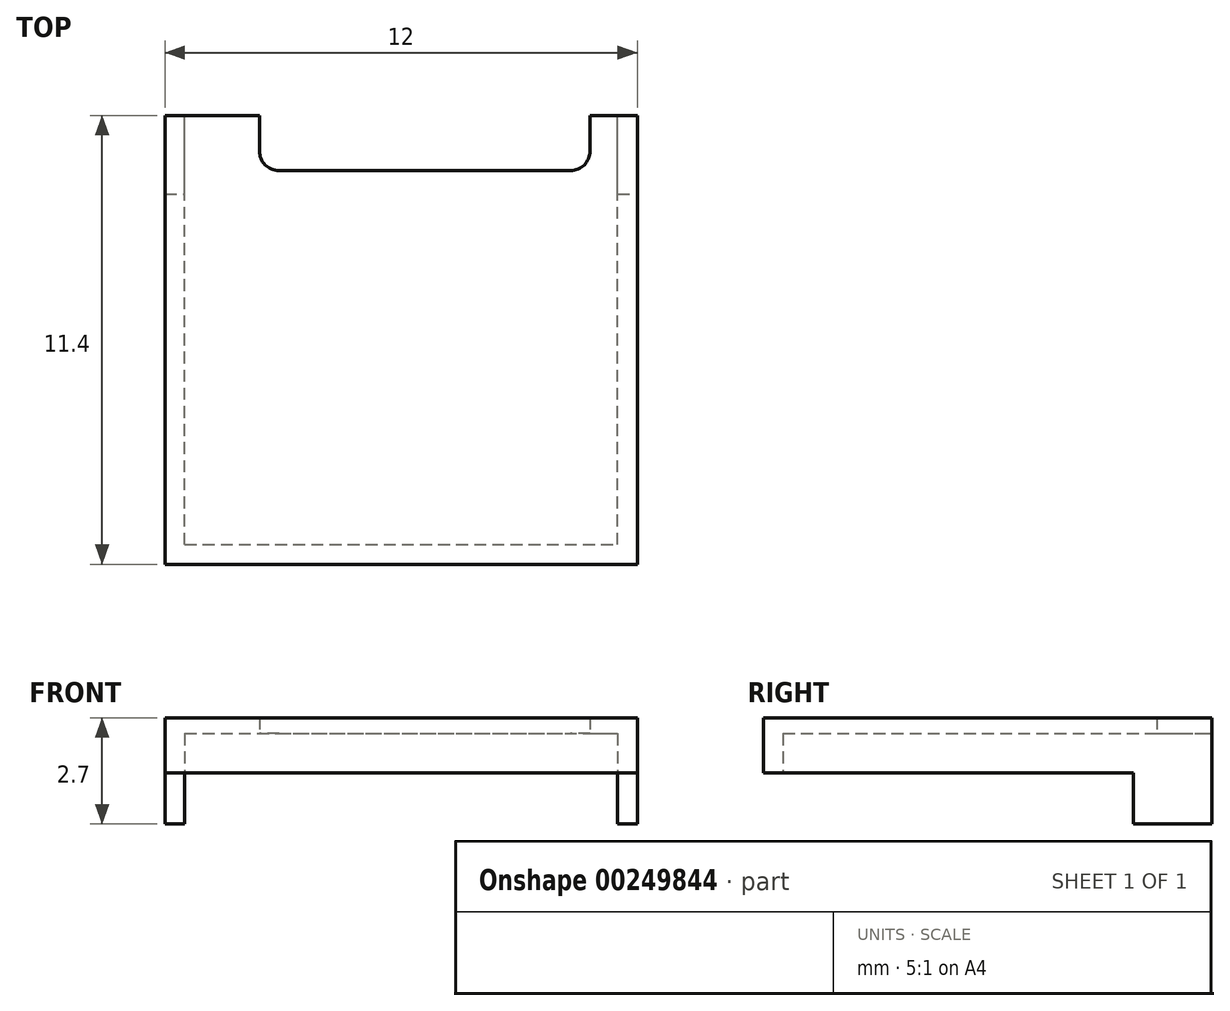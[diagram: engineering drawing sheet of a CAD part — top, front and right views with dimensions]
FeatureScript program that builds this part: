
annotation { "Feature Type Name" : "Feature", "Feature Type Description" : "" }
export const myFeature = defineFeature(function(context is Context, id is Id, definition is map)
    precondition{}
    {
        {
            var Q0;
            Q0=qCreatedBy(makeId("Top.planeOp"),FACE);
            var sketch = newSketch(context, id + "F0", { "sketchPlane" : qUnion([Q0])});
            skLineSegment(sketch, "E0.bottom", {"start": v(0, 0) * mm, "end": v(12, 0) * mm});
            skLineSegment(sketch, "E0.top", {"start": v(0, 11.4) * mm, "end": v(2.4, 11.4) * mm});
            skLineSegment(sketch, "E0.left", {"start": v(0, 0) * mm, "end": v(0, 11.4) * mm});
            skLineSegment(sketch, "E0.right", {"start": v(12, 0) * mm, "end": v(12, 11.4) * mm});
            skLineSegment(sketch, "E1", {"start": v(2.4, 11.4) * mm, "end": v(2.4, 10) * mm});
            skLineSegment(sketch, "E2", {"start": v(2.4, 10) * mm, "end": v(10.8, 10) * mm});
            skLineSegment(sketch, "E3", {"start": v(10.8, 10) * mm, "end": v(10.8, 11.4) * mm});
            skLineSegment(sketch, "E4.trimOffspring", {"start": v(10.8, 11.4) * mm, "end": v(12, 11.4) * mm});
            skSolve(sketch);
        }
        {
            var Q0;
            Q0 = qSketchRegion(id + "F0", true);
            extrude(context, id + "F1", {"entities" : qUnion([Q0]), "depth" : 1.4 * mm});
        }
        {
            var Q0;
            Q0=makeQuery(id+"F1.opExtrude","CAP_FACE",FACE,{"disambiguationData":[OSD([sQuery(id+"F0.wireOp",EDGE,"E0.bottom"),sQuery(id+"F0.wireOp",EDGE,"E0.top"),sQuery(id+"F0.wireOp",EDGE,"E0.left"),sQuery(id+"F0.wireOp",EDGE,"E0.right"),sQuery(id+"F0.wireOp",EDGE,"E1"),sQuery(id+"F0.wireOp",EDGE,"E2"),sQuery(id+"F0.wireOp",EDGE,"E3"),sQuery(id+"F0.wireOp",EDGE,"E4.trimOffspring")])],"isStart":true});
            var sketch = newSketch(context, id + "F2", { "sketchPlane" : qUnion([Q0])});
            skLineSegment(sketch, "E5", {"start": v(0.5, -0.5) * mm, "end": v(11.5, -0.5) * mm});
            skLineSegment(sketch, "E6", {"start": v(11.5, -0.5) * mm, "end": v(11.5, -11.4) * mm});
            skLineSegment(sketch, "E7", {"start": v(0.5, -11.4) * mm, "end": v(2.4, -11.4) * mm});
            skLineSegment(sketch, "E8", {"start": v(2.4, -11.4) * mm, "end": v(2.4, -10) * mm});
            skLineSegment(sketch, "E9", {"start": v(2.4, -10) * mm, "end": v(10.8, -10) * mm});
            skLineSegment(sketch, "E10", {"start": v(10.8, -10) * mm, "end": v(10.8, -11.4) * mm});
            skLineSegment(sketch, "E11", {"start": v(10.8, -11.4) * mm, "end": v(11.5, -11.4) * mm});
            skLineSegment(sketch, "E12", {"start": v(0.5, -0.5) * mm, "end": v(0.5, -11.4) * mm});
            skSolve(sketch);
        }
        {
            var Q0;
            Q0 = qSketchRegion(id + "F2", true);
            extrude(context, id + "F3", {"entities" : qUnion([Q0]), "operationType" : NewBodyOperationType.REMOVE, "oppositeDirection" : true, "depth" : 1 * mm});
        }
        {
            var Q0;
            Q0=makeQuery(id+"F1.opExtrude","CAP_FACE",FACE,{"disambiguationData":[OSD([sQuery(id+"F0.wireOp",EDGE,"E0.bottom"),sQuery(id+"F0.wireOp",EDGE,"E0.top"),sQuery(id+"F0.wireOp",EDGE,"E0.left"),sQuery(id+"F0.wireOp",EDGE,"E0.right"),sQuery(id+"F0.wireOp",EDGE,"E1"),sQuery(id+"F0.wireOp",EDGE,"E2"),sQuery(id+"F0.wireOp",EDGE,"E3"),sQuery(id+"F0.wireOp",EDGE,"E4.trimOffspring")])],"isStart":true});
            var sketch = newSketch(context, id + "F4", { "sketchPlane" : qUnion([Q0])});
            skLineSegment(sketch, "E13.bottom", {"start": v(0, -11.4) * mm, "end": v(0.5, -11.4) * mm});
            skLineSegment(sketch, "E13.top", {"start": v(0, -9.4) * mm, "end": v(0.5, -9.4) * mm});
            skLineSegment(sketch, "E13.left", {"start": v(0, -11.4) * mm, "end": v(0, -9.4) * mm});
            skLineSegment(sketch, "E13.right", {"start": v(0.5, -11.4) * mm, "end": v(0.5, -9.4) * mm});
            skLineSegment(sketch, "E14.bottom", {"start": v(11.5, -11.4) * mm, "end": v(12, -11.4) * mm});
            skLineSegment(sketch, "E14.top", {"start": v(11.5, -9.4) * mm, "end": v(12, -9.4) * mm});
            skLineSegment(sketch, "E14.left", {"start": v(11.5, -11.4) * mm, "end": v(11.5, -9.4) * mm});
            skLineSegment(sketch, "E14.right", {"start": v(12, -11.4) * mm, "end": v(12, -9.4) * mm});
            skSolve(sketch);
        }
        {
            var Q0;
            Q0 = qSketchRegion(id + "F4", true);
            extrude(context, id + "F5", {"entities" : qUnion([Q0]), "operationType" : NewBodyOperationType.ADD, "depth" : 1.3 * mm});
        }
        {
            var Q0;
            Q0=makeQuery(id+"F1.opExtrude","SWEPT_EDGE",EDGE,{"disambiguationData":[OSD([sQuery(id+"F0.wireOp",EDGE,"E2"),sQuery(id+"F0.wireOp",EDGE,"E3")])]});
            var Q1;
            Q1=makeQuery(id+"F1.opExtrude","SWEPT_EDGE",EDGE,{"disambiguationData":[OSD([sQuery(id+"F0.wireOp",EDGE,"E1"),sQuery(id+"F0.wireOp",EDGE,"E2")])]});
            fillet(context, id + "F6", {"entities" : qUnion([Q0, Q1]), "radius" : 0.5 * mm, "tangentPropagation" : true, "allowEdgeOverflow" : false});
        }
    });
